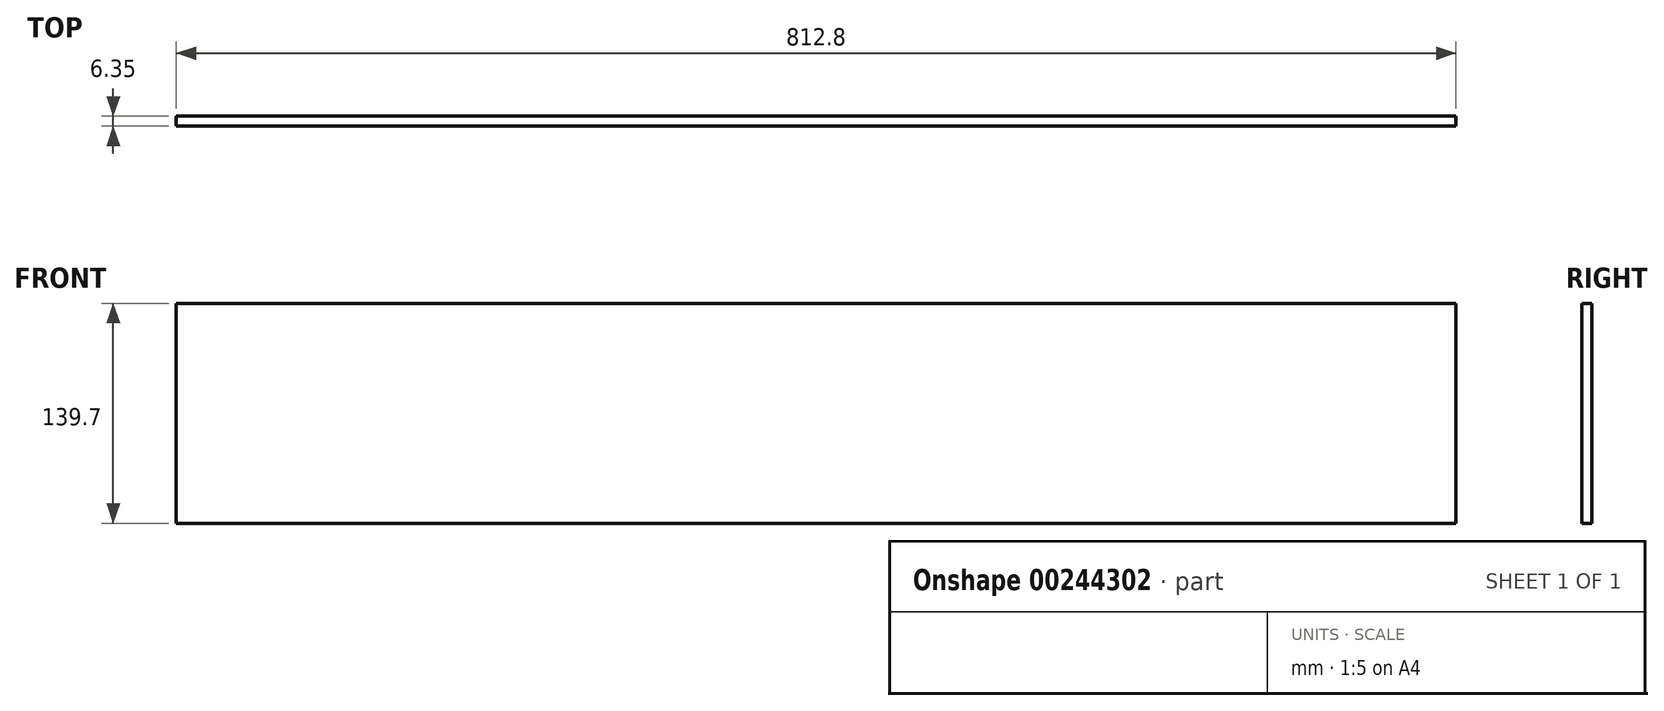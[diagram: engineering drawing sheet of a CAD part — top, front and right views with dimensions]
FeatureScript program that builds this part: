
annotation { "Feature Type Name" : "Feature", "Feature Type Description" : "" }
export const myFeature = defineFeature(function(context is Context, id is Id, definition is map)
    precondition{}
    {
        {
            var Q0;
            Q0=qCreatedBy(makeId("Front.planeOp"),FACE);
            var sketch = newSketch(context, id + "F0", { "sketchPlane" : qUnion([Q0])});
            skLineSegment(sketch, "E0.bottom", {"start": v(-301.99, 72.87) * mm, "end": v(510.81, 72.87) * mm});
            skLineSegment(sketch, "E0.top", {"start": v(-301.99, -66.83) * mm, "end": v(510.81, -66.83) * mm});
            skLineSegment(sketch, "E0.left", {"start": v(-301.99, 72.87) * mm, "end": v(-301.99, -66.83) * mm});
            skLineSegment(sketch, "E0.right", {"start": v(510.81, 72.87) * mm, "end": v(510.81, -66.83) * mm});
            skSolve(sketch);
        }
        {
            var Q0;
            Q0 = qSketchRegion(id + "F0", true);
            extrude(context, id + "F1", {"entities" : qUnion([Q0]), "depth" : 6.35 * mm});
        }
    });
